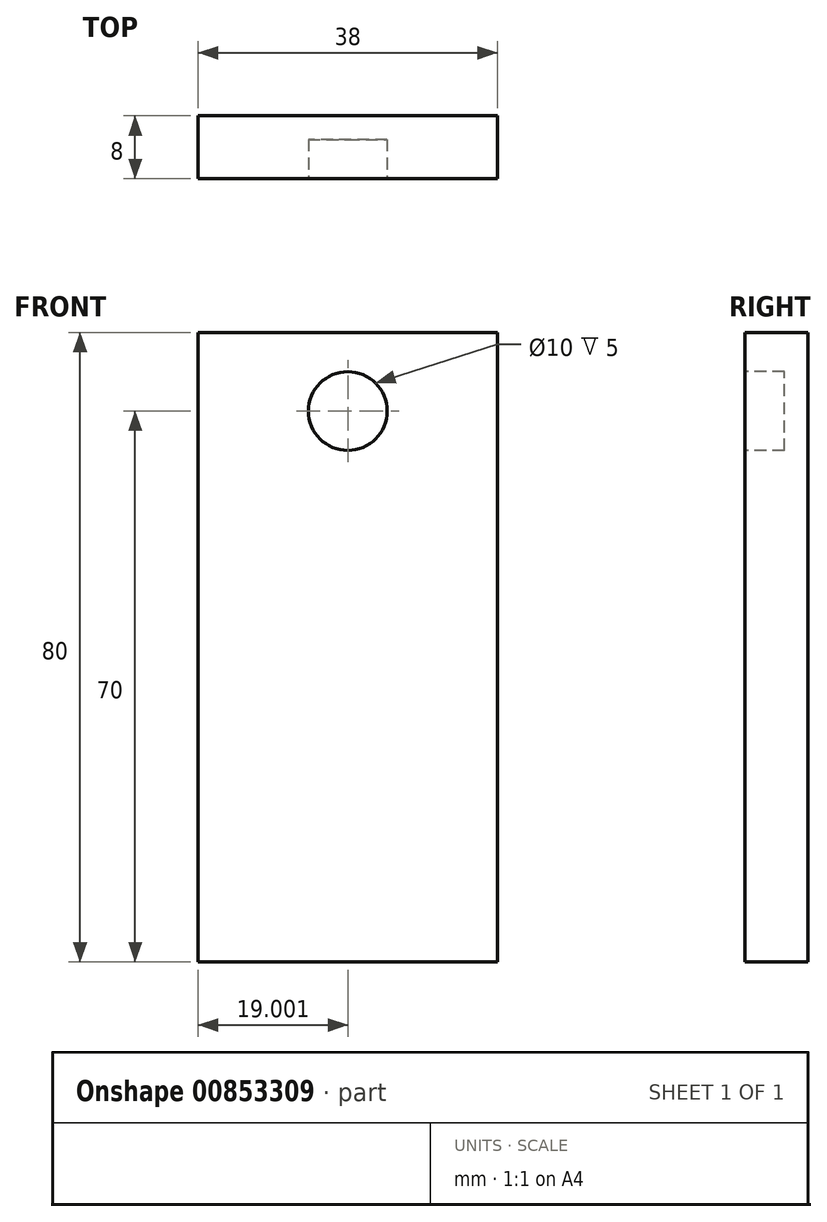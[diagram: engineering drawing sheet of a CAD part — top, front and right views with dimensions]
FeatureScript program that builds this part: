
annotation { "Feature Type Name" : "Feature", "Feature Type Description" : "" }
export const myFeature = defineFeature(function(context is Context, id is Id, definition is map)
    precondition{}
    {
        {
            var Q0;
            Q0=qCreatedBy(makeId("Top.planeOp"),FACE);
            var sketch = newSketch(context, id + "F0", { "sketchPlane" : qUnion([Q0])});
            skLineSegment(sketch, "E0.bottom", {"start": v(-13.7, -12.4) * mm, "end": v(24.3, -12.4) * mm});
            skLineSegment(sketch, "E0.top", {"start": v(-13.7, -20.4) * mm, "end": v(24.3, -20.4) * mm});
            skLineSegment(sketch, "E0.left", {"start": v(-13.7, -12.4) * mm, "end": v(-13.7, -20.4) * mm});
            skLineSegment(sketch, "E0.right", {"start": v(24.3, -12.4) * mm, "end": v(24.3, -20.4) * mm});
            skSolve(sketch);
        }
        {
            var Q0;
            Q0=makeQuery(id+"F0.imprint","IMPRINT",FACE,{"disambiguationData":[TD([[makeQuery(id+"F0.imprint","IMPRINT",EDGE,{"derivedFrom":sQuery(id+"F0.wireOp",EDGE,"E0.bottom")}),-1.0]])]});
            extrude(context, id + "F1", {"entities" : qUnion([Q0]), "depth" : 80 * mm, "offsetDistance" : 25 * mm});
        }
        {
            var Q0;
            Q0=makeQuery(id+"F1.opExtrude","SWEPT_FACE",FACE,{"disambiguationData":[OSD([sQuery(id+"F0.wireOp",EDGE,"E0.top")])]});
            var sketch = newSketch(context, id + "F2", { "sketchPlane" : qUnion([Q0])});
            skCircle(sketch, "E1", {"center": v(5.3, 70) * mm, "radius": 5 * mm});
            skSolve(sketch);
        }
        {
            var Q0;
            Q0 = qSketchRegion(id + "F2", true);
            extrude(context, id + "F3", {"entities" : qUnion([Q0]), "operationType" : NewBodyOperationType.REMOVE, "oppositeDirection" : true, "depth" : 5 * mm, "offsetDistance" : 25 * mm});
        }
    });
